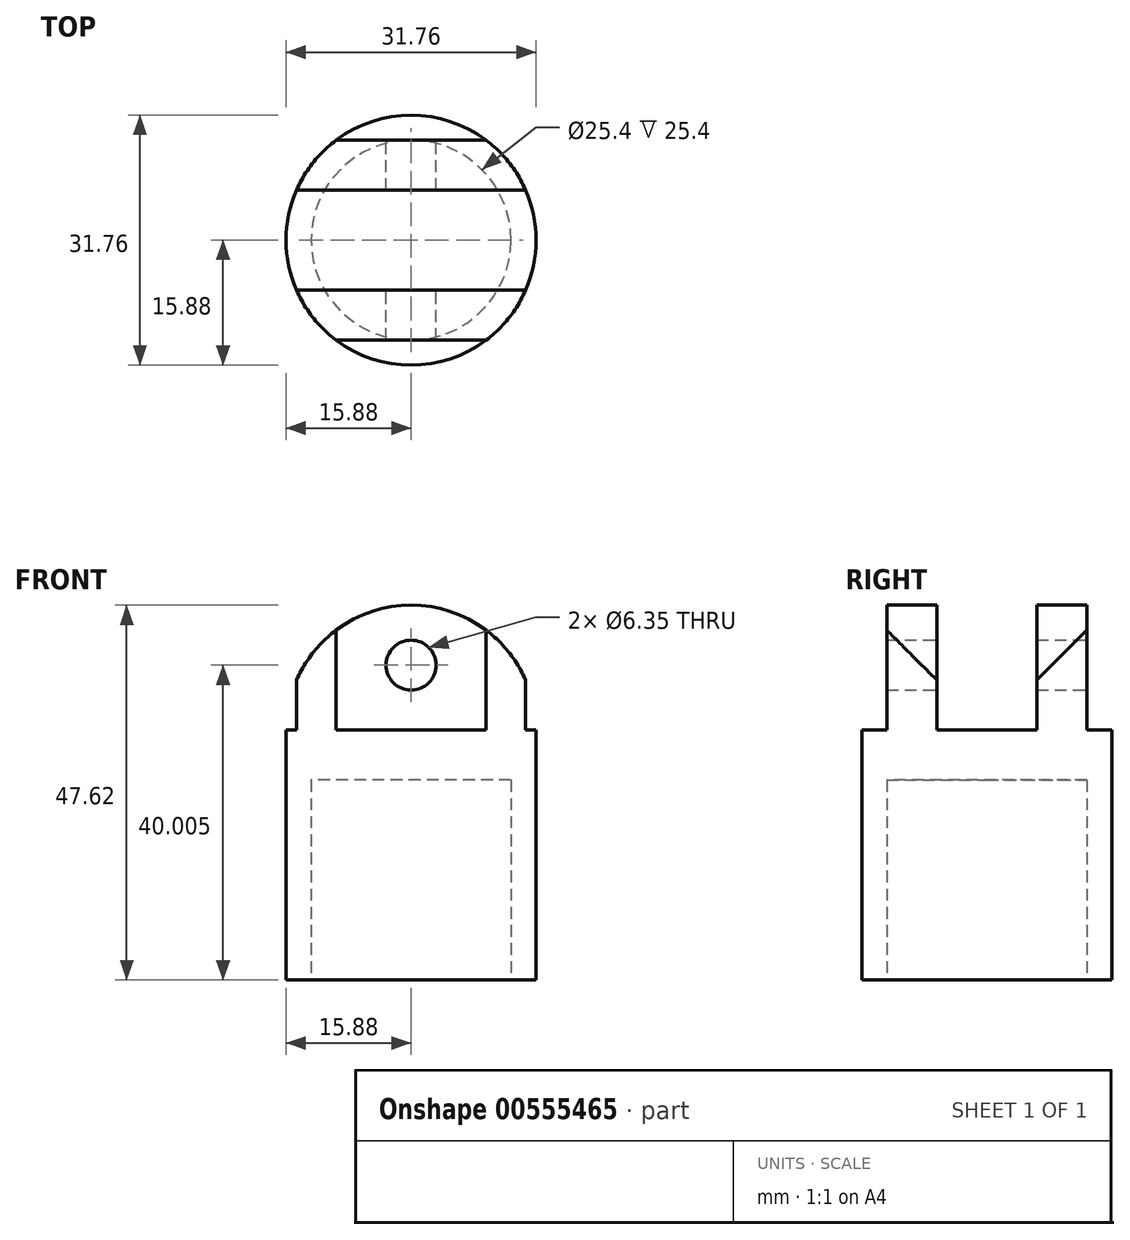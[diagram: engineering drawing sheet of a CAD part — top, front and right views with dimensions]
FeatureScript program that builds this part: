
annotation { "Feature Type Name" : "Feature", "Feature Type Description" : "" }
export const myFeature = defineFeature(function(context is Context, id is Id, definition is map)
    precondition{}
    {
        {
            var Q0;
            Q0=qCreatedBy(makeId("Top.planeOp"),FACE);
            var sketch = newSketch(context, id + "F0", { "sketchPlane" : qUnion([Q0])});
            skCircle(sketch, "E0", {"center": v(0, 0) * mm, "radius": 15.88 * mm});
            skCircle(sketch, "E1", {"center": v(0, 0) * mm, "radius": 12.7 * mm});
            skSolve(sketch);
        }
        {
            var Q0;
            Q0=makeQuery(id+"F0.imprint","IMPRINT",FACE,{"disambiguationData":[TD([[makeQuery(id+"F0.imprint","IMPRINT",EDGE,{"derivedFrom":sQuery(id+"F0.wireOp",EDGE,"E0")}),1.0]])]});
            extrude(context, id + "F1", {"entities" : qUnion([Q0]), "depth" : 25.4 * mm, "offsetDistance" : 25.4 * mm});
        }
        {
            var Q0;
            Q0=makeQuery(id+"F1.opExtrude","CAP_FACE",FACE,{"disambiguationData":[OSD([sQuery(id+"F0.wireOp",EDGE,"E0"),sQuery(id+"F0.wireOp",EDGE,"E1")])],"isStart":false});
            var sketch = newSketch(context, id + "F2", { "sketchPlane" : qUnion([Q0])});
            skCircle(sketch, "E2", {"center": v(0, 0) * mm, "radius": 15.88 * mm});
            skSolve(sketch);
        }
        {
            var Q0;
            Q0=qSketchRegion(id+"F2",true);
            extrude(context, id + "F3", {"entities" : qUnion([Q0]), "operationType" : NewBodyOperationType.ADD, "depth" : 6.35 * mm, "offsetDistance" : 25.4 * mm});
        }
        {
            var Q0;
            Q0=qCreatedBy(makeId("Front.planeOp"),FACE);
            var sketch = newSketch(context, id + "F4", { "sketchPlane" : qUnion([Q0])});
            skLineSegment(sketch, "E3.bottom", {"start": v(-15.88, 31.75) * mm, "end": v(15.88, 31.75) * mm});
            skLineSegment(sketch, "E3.top", {"start": v(-15.88, 25.4) * mm, "end": v(15.88, 25.4) * mm});
            skLineSegment(sketch, "E3.left", {"start": v(-15.88, 31.75) * mm, "end": v(-15.88, 25.4) * mm});
            skLineSegment(sketch, "E3.right", {"start": v(15.88, 31.75) * mm, "end": v(15.88, 25.4) * mm});
            skArc(sketch, "E4", {"start": v(15.88, 31.75) * mm, "mid": v(0, 47.62) * mm, "end": v(-15.88, 31.75) * mm});
            skCircle(sketch, "E5", {"center": v(0, 40) * mm, "radius": 3.18 * mm});
            skSolve(sketch);
        }
        {
            var Q0;
            Q0=makeQuery(id+"F4.imprint","IMPRINT",FACE,{"disambiguationData":[TD([[makeQuery(id+"F4.imprint","IMPRINT",EDGE,{"derivedFrom":sQuery(id+"F4.wireOp",EDGE,"E3.bottom")}),1.0]])]});
            extrude(context, id + "F5", {"entities" : qUnion([Q0]), "operationType" : NewBodyOperationType.ADD, "depth" : 12.7 * mm, "offsetDistance" : 25.4 * mm, "hasSecondDirection" : true, "secondDirectionOppositeDirection" : true, "secondDirectionDepth" : 12.7 * mm});
        }
        {
            var Q0;
            Q0=qCreatedBy(makeId("Front.planeOp"),FACE);
            var sketch = newSketch(context, id + "F6", { "sketchPlane" : qUnion([Q0])});
            skLineSegment(sketch, "E6.bottom", {"start": v(-15.88, 0) * mm, "end": v(-37.34, 0) * mm});
            skLineSegment(sketch, "E6.top", {"start": v(-15.88, 60.37) * mm, "end": v(-37.34, 60.37) * mm});
            skLineSegment(sketch, "E6.left", {"start": v(-15.88, 0) * mm, "end": v(-15.88, 60.37) * mm});
            skLineSegment(sketch, "E6.right", {"start": v(-37.34, 0) * mm, "end": v(-37.34, 60.37) * mm});
            skLineSegment(sketch, "E7", {"start": v(0, -10.16) * mm, "end": v(0, 70.36) * mm});
            skSolve(sketch);
        }
        {
            var Q0;
            Q0=makeQuery(id+"F6.imprint","IMPRINT",FACE,{"disambiguationData":[TD([[makeQuery(id+"F6.imprint","IMPRINT",EDGE,{"derivedFrom":sQuery(id+"F6.wireOp",EDGE,"E6.bottom")}),-1.0]])]});
            var Q1;
            Q1=sQuery(id+"F6.wireOp",EDGE,"E7");
            revolve(context, id + "F7", {"operationType" : NewBodyOperationType.REMOVE, "entities" : qUnion([Q0]), "axis" : qUnion([Q1]), "revolveType" : RevolveType.FULL, "oppositeDirection" : true});
        }
        {
            var Q0;
            Q0=qCreatedBy(makeId("Right.planeOp"),FACE);
            var sketch = newSketch(context, id + "F8", { "sketchPlane" : qUnion([Q0])});
            skLineSegment(sketch, "E8.bottom", {"start": v(6.35, 59.7) * mm, "end": v(-6.35, 59.7) * mm});
            skLineSegment(sketch, "E8.top", {"start": v(6.35, 31.75) * mm, "end": v(-6.35, 31.75) * mm});
            skLineSegment(sketch, "E8.left", {"start": v(6.35, 59.7) * mm, "end": v(6.35, 31.75) * mm});
            skLineSegment(sketch, "E8.right", {"start": v(-6.35, 59.7) * mm, "end": v(-6.35, 31.75) * mm});
            skSolve(sketch);
        }
        {
            var Q0;
            Q0=qSketchRegion(id+"F8",true);
            extrude(context, id + "F9", {"entities" : qUnion([Q0]), "operationType" : NewBodyOperationType.REMOVE, "oppositeDirection" : true, "depth" : 25.4 * mm, "offsetDistance" : 25.4 * mm, "hasSecondDirection" : true, "secondDirectionOppositeDirection" : false, "secondDirectionDepth" : 25.4 * mm});
        }
    });
